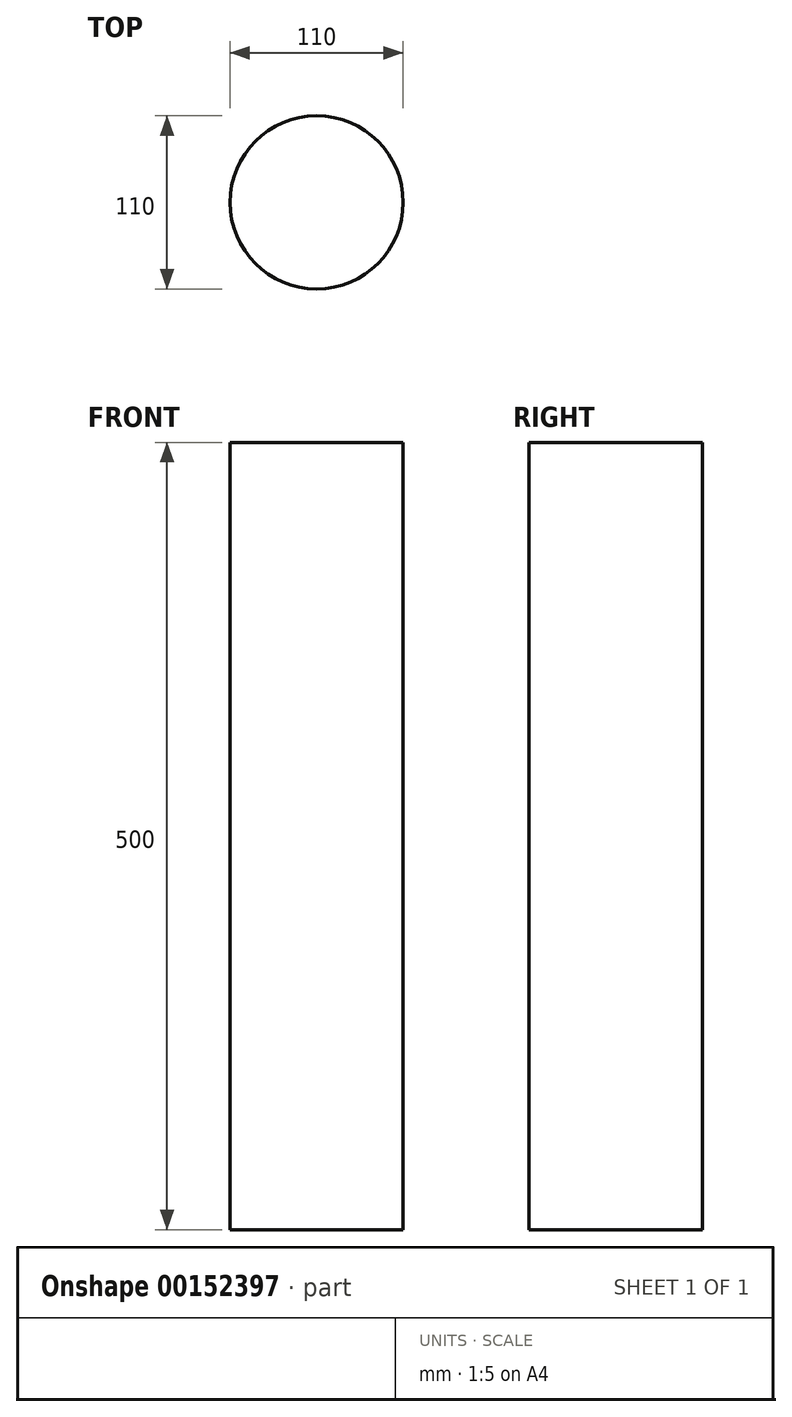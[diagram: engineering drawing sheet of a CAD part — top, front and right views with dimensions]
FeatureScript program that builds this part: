
annotation { "Feature Type Name" : "Feature", "Feature Type Description" : "" }
export const myFeature = defineFeature(function(context is Context, id is Id, definition is map)
    precondition{}
    {
        {
            var Q0;
            Q0=qCreatedBy(makeId("Top.planeOp"),FACE);
            var sketch = newSketch(context, id + "F0", { "sketchPlane" : qUnion([Q0])});
            skCircle(sketch, "E0", {"center": v(0, 0) * mm, "radius": 55 * mm});
            skCircle(sketch, "E1", {"center": v(0, 0) * mm, "radius": 50 * mm});
            skSolve(sketch);
        }
        {
            var Q0;
            Q0=makeQuery(id+"F0.imprint","IMPRINT",FACE,{"disambiguationData":[TD([[makeQuery(id+"F0.imprint","IMPRINT",EDGE,{"derivedFrom":sQuery(id+"F0.wireOp",EDGE,"E0")}),1.0]])]});
            var Q1;
            Q1=makeQuery(id+"F0.imprint","IMPRINT",FACE,{"disambiguationData":[TD([[makeQuery(id+"F0.imprint","IMPRINT",EDGE,{"derivedFrom":sQuery(id+"F0.wireOp",EDGE,"E1")}),1.0]])]});
            extrude(context, id + "F1", {"entities" : qUnion([Q0, Q1]), "oppositeDirection" : true, "depth" : 500 * mm});
        }
        {
            var Q0;
            Q0=makeQuery(id+"F0.imprint","IMPRINT",FACE,{"disambiguationData":[TD([[makeQuery(id+"F0.imprint","IMPRINT",EDGE,{"derivedFrom":sQuery(id+"F0.wireOp",EDGE,"E0")}),1.0]])]});
            extrude(context, id + "F2", {"entities" : qUnion([Q0]), "operationType" : NewBodyOperationType.ADD, "oppositeDirection" : true, "depth" : 62.5 * mm});
        }
    });
